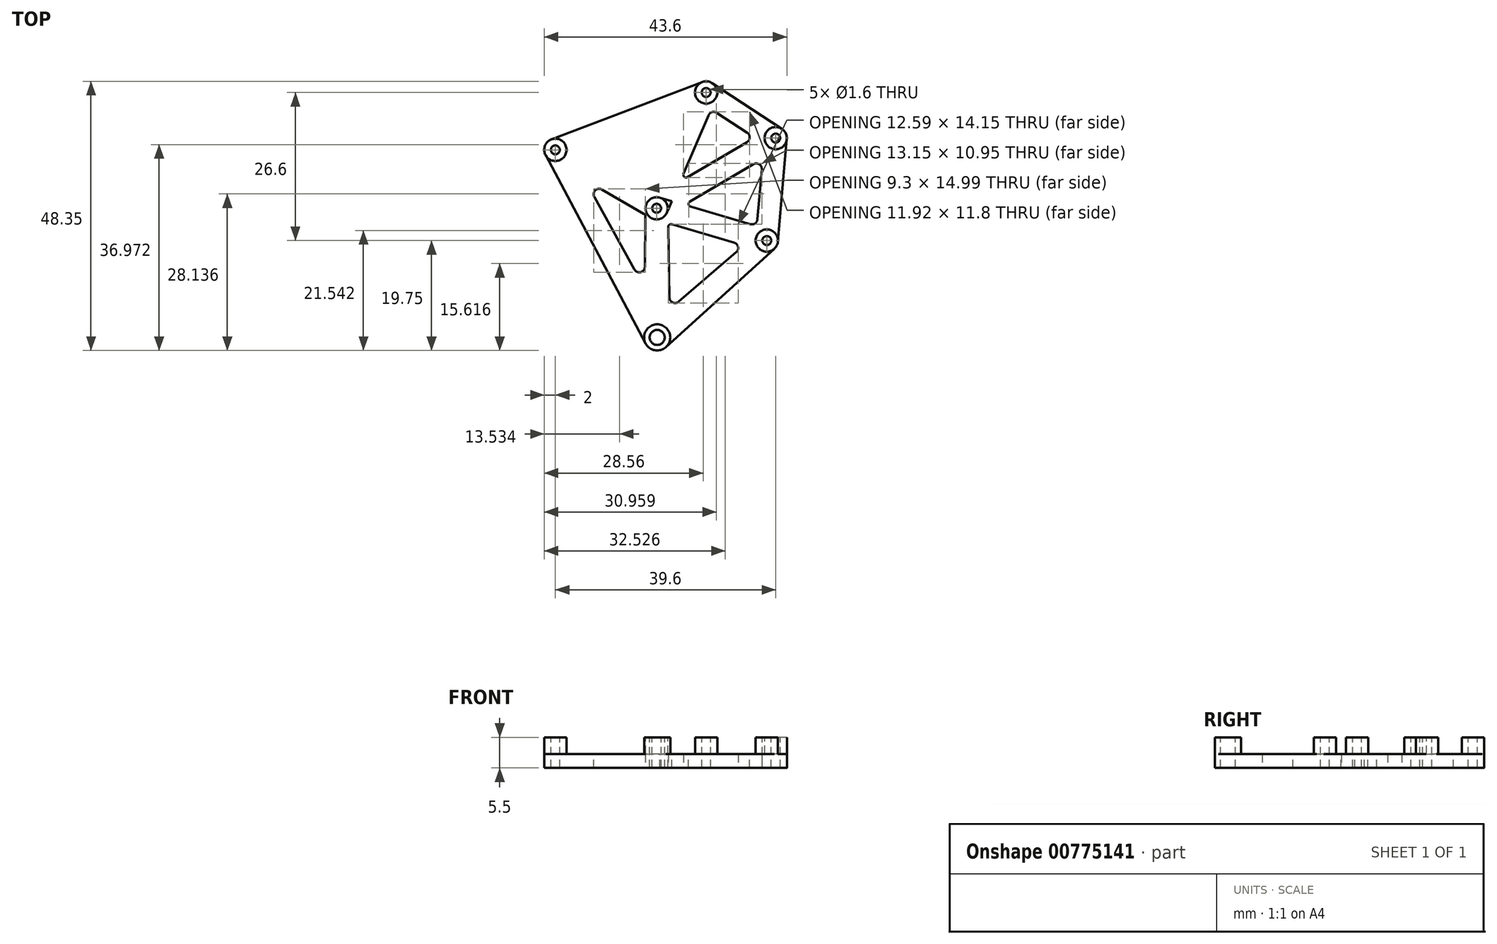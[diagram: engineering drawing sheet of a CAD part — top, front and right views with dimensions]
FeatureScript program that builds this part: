
annotation { "Feature Type Name" : "Feature", "Feature Type Description" : "" }
export const myFeature = defineFeature(function(context is Context, id is Id, definition is map)
    precondition{}
    {
        {
            var Q0;
            Q0=qCreatedBy(makeId("Top.planeOp"),FACE);
            var sketch = newSketch(context, id + "F0", { "sketchPlane" : qUnion([Q0])});
            skCircle(sketch, "E0", {"center": v(4.2, 40) * mm, "radius": 0.8 * mm});
            skCircle(sketch, "E1", {"center": v(31.3, 50.3) * mm, "radius": 0.8 * mm});
            skCircle(sketch, "E2", {"center": v(43.8, 42.1) * mm, "radius": 0.8 * mm});
            skCircle(sketch, "E3", {"center": v(22.4, 29.5) * mm, "radius": 0.8 * mm});
            skCircle(sketch, "E4", {"center": v(22.5, 6.3) * mm, "radius": 1.35 * mm});
            skCircle(sketch, "E5", {"center": v(42.2, 23.7) * mm, "radius": 0.8 * mm});
            skSolve(sketch);
        }
        {
            var Q0;
            Q0=qCreatedBy(makeId("Top.planeOp"),FACE);
            var sketch = newSketch(context, id + "F1", { "sketchPlane" : qUnion([Q0])});
            skCircle(sketch, "E6.0", {"center": v(4.2, 40) * mm, "radius": 0.8 * mm});
            skPoint(sketch, "E7.0", {"position": v(22.4, 29.5) * mm});
            skPoint(sketch, "E8.0", {"position": v(31.3, 50.3) * mm});
            skCircle(sketch, "E9.0", {"center": v(31.3, 50.3) * mm, "radius": 0.8 * mm});
            skCircle(sketch, "E10.0", {"center": v(43.8, 42.1) * mm, "radius": 0.8 * mm});
            skCircle(sketch, "E11.0", {"center": v(22.4, 29.5) * mm, "radius": 0.8 * mm});
            skCircle(sketch, "E12.0", {"center": v(42.2, 23.7) * mm, "radius": 0.8 * mm});
            skCircle(sketch, "E13.0", {"center": v(22.5, 6.3) * mm, "radius": 1.35 * mm});
            skLineSegment(sketch, "E14", {"start": v(4.2, 40) * mm, "end": v(22.4, 29.5) * mm, "construction": true});
            skLineSegment(sketch, "E15", {"start": v(31.3, 50.3) * mm, "end": v(22.4, 29.5) * mm, "construction": true});
            skLineSegment(sketch, "E16", {"start": v(22.4, 29.5) * mm, "end": v(42.2, 23.7) * mm, "construction": true});
            skLineSegment(sketch, "E17", {"start": v(22.4, 29.5) * mm, "end": v(22.5, 6.3) * mm, "construction": true});
            skLineSegment(sketch, "E18", {"start": v(22.4, 29.5) * mm, "end": v(43.8, 42.1) * mm, "construction": true});
            skLineSegment(sketch, "E19", {"start": v(43.8, 42.1) * mm, "end": v(42.2, 23.7) * mm, "construction": true});
            skLineSegment(sketch, "E20", {"start": v(22.5, 6.3) * mm, "end": v(42.2, 23.7) * mm, "construction": true});
            skLineSegment(sketch, "E21", {"start": v(43.8, 42.1) * mm, "end": v(31.3, 50.3) * mm});
            skLineSegment(sketch, "E22", {"start": v(31.3, 50.3) * mm, "end": v(4.2, 40) * mm, "construction": true});
            skLineSegment(sketch, "E23", {"start": v(4.2, 40) * mm, "end": v(22.5, 6.3) * mm, "construction": true});
            skLineSegment(sketch, "E24", {"start": v(5.2, 41.73) * mm, "end": v(23.4, 31.23) * mm});
            skLineSegment(sketch, "E25", {"start": v(3.2, 38.27) * mm, "end": v(21.4, 27.77) * mm});
            skArc(sketch, "E26", {"start": v(5.2, 41.73) * mm, "mid": v(2.47, 41) * mm, "end": v(3.2, 38.27) * mm});
            skArc(sketch, "E27", {"start": v(21.4, 27.77) * mm, "mid": v(24.13, 28.5) * mm, "end": v(23.4, 31.23) * mm});
            skLineSegment(sketch, "E28", {"start": v(20.4, 29.52) * mm, "end": v(20.15, 6.33) * mm});
            skLineSegment(sketch, "E29", {"start": v(24.4, 29.54) * mm, "end": v(24.85, 6.35) * mm});
            skArc(sketch, "E30", {"start": v(20.15, 6.33) * mm, "mid": v(20.22, 5.74) * mm, "end": v(20.42, 5.2) * mm});
            skArc(sketch, "E31", {"start": v(20.4, 29.52) * mm, "mid": v(22.4, 31.5) * mm, "end": v(24.4, 29.54) * mm});
            skLineSegment(sketch, "E32", {"start": v(2.43, 39.06) * mm, "end": v(20.42, 5.2) * mm});
            skCircle(sketch, "E33", {"center": v(22.5, 6.3) * mm, "radius": 2.35 * mm});
            skCircle(sketch, "E34", {"center": v(4.2, 40) * mm, "radius": 2 * mm});
            skLineSegment(sketch, "E35", {"start": v(5.95, 40.97) * mm, "end": v(24.55, 7.44) * mm});
            skCircle(sketch, "E36", {"center": v(42.2, 23.7) * mm, "radius": 2 * mm});
            skCircle(sketch, "E37", {"center": v(22.4, 29.5) * mm, "radius": 2 * mm});
            skLineSegment(sketch, "E38", {"start": v(42.76, 25.62) * mm, "end": v(22.96, 31.42) * mm});
            skLineSegment(sketch, "E39", {"start": v(41.64, 21.78) * mm, "end": v(21.84, 27.58) * mm});
            skLineSegment(sketch, "E40", {"start": v(24.08, 4.56) * mm, "end": v(43.54, 22.22) * mm});
            skLineSegment(sketch, "E41", {"start": v(20.97, 8.08) * mm, "end": v(40.9, 25.22) * mm});
            skCircle(sketch, "E42", {"center": v(43.8, 42.1) * mm, "radius": 2 * mm});
            skCircle(sketch, "E43", {"center": v(31.3, 50.3) * mm, "radius": 2 * mm});
            skLineSegment(sketch, "E44", {"start": v(45.8, 41.93) * mm, "end": v(44.2, 23.53) * mm});
            skLineSegment(sketch, "E45", {"start": v(40.2, 23.87) * mm, "end": v(41.8, 42.27) * mm});
            skLineSegment(sketch, "E46", {"start": v(32.4, 51.97) * mm, "end": v(44.9, 43.77) * mm});
            skLineSegment(sketch, "E47", {"start": v(30.2, 48.63) * mm, "end": v(42.7, 40.43) * mm});
            skLineSegment(sketch, "E48", {"start": v(21.39, 31.22) * mm, "end": v(42.79, 43.82) * mm});
            skLineSegment(sketch, "E49", {"start": v(44.81, 40.38) * mm, "end": v(23.41, 27.78) * mm});
            skLineSegment(sketch, "E50", {"start": v(29.46, 51.09) * mm, "end": v(20.56, 30.29) * mm});
            skLineSegment(sketch, "E51", {"start": v(33.14, 49.51) * mm, "end": v(24.24, 28.71) * mm});
            skLineSegment(sketch, "E52", {"start": v(5.15, 38.24) * mm, "end": v(32, 48.43) * mm});
            skLineSegment(sketch, "E53", {"start": v(3.49, 41.87) * mm, "end": v(30.59, 52.17) * mm});
            skPoint(sketch, "E54.end.orphan", {"position": v(23.62, 4.23) * mm});
            skArc(sketch, "E55.trimOffspring", {"start": v(24.08, 4.56) * mm, "mid": v(24.66, 5.37) * mm, "end": v(24.85, 6.35) * mm});
            skPoint(sketch, "E56.end.orphan", {"position": v(23.14, 5.11) * mm});
            skSolve(sketch);
        }
        {
            var Q0;
            Q0=makeQuery(id+"F1.imprint","IMPRINT",FACE,{"disambiguationData":[TD([[makeQuery(id+"F1.imprint","IMPRINT",EDGE,{"derivedFrom":sQuery(id+"F1.wireOp",EDGE,"E6.0")}),-1.0]])]});
            var Q1;
            {var subQ3=sQuery(id+"F1.wireOp",EDGE,"E53");Q1=makeQuery(id+"F1.imprint","IMPRINT",FACE,{"disambiguationData":[TD([[makeQuery(id+"F1.imprint","IMPRINT",EDGE,{"derivedFrom":subQ3}),-1.0]])]});}
            var Q2;
            Q2=makeQuery(id+"F1.imprint","IMPRINT",FACE,{"disambiguationData":[TD([[makeQuery(id+"F1.imprint","IMPRINT",EDGE,{"derivedFrom":sQuery(id+"F1.wireOp",EDGE,"E9.0")}),-1.0]])]});
            var Q3;
            Q3=makeQuery(id+"F1.imprint","IMPRINT",FACE,{"disambiguationData":[TD([[makeQuery(id+"F1.imprint","IMPRINT",EDGE,{"derivedFrom":sQuery(id+"F1.wireOp",EDGE,"E13.0")}),-1.0]])]});
            var Q4;
            Q4=makeQuery(id+"F1.imprint","IMPRINT",FACE,{"disambiguationData":[TD([[makeQuery(id+"F1.imprint","IMPRINT",EDGE,{"derivedFrom":sQuery(id+"F1.wireOp",EDGE,"E12.0")}),-1.0]])]});
            var Q5;
            Q5=makeQuery(id+"F1.imprint","IMPRINT",FACE,{"disambiguationData":[TD([[makeQuery(id+"F1.imprint","IMPRINT",EDGE,{"derivedFrom":sQuery(id+"F1.wireOp",EDGE,"E10.0")}),-1.0]])]});
            var Q6;
            Q6=makeQuery(id+"F1.imprint","IMPRINT",FACE,{"disambiguationData":[TD([[makeQuery(id+"F1.imprint","IMPRINT",EDGE,{"derivedFrom":sQuery(id+"F1.wireOp",EDGE,"E11.0")}),-1.0]])]});
            var Q7;
            {var subQ3=sQuery(id+"F1.wireOp",EDGE,"E40");Q7=makeQuery(id+"F1.imprint","IMPRINT",FACE,{"disambiguationData":[TD([[makeQuery(id+"F1.imprint","IMPRINT",EDGE,{"derivedFrom":subQ3}),1.0]])]});}
            var Q8;
            {var subQ0=sQuery(id+"F1.wireOp",EDGE,"E44");Q8=makeQuery(id+"F1.imprint","IMPRINT",FACE,{"disambiguationData":[TD([[makeQuery(id+"F1.imprint","IMPRINT",EDGE,{"derivedFrom":subQ0}),-1.0]])]});}
            var Q9;
            {var subQ0=sQuery(id+"F1.wireOp",EDGE,"E33");var subQ1=sQuery(id+"F1.wireOp",EDGE,"E29");var subQ2=makeQuery(id+"F1.imprint","INTERSECT",VERTEX,{"derivedFrom":[subQ1,subQ0]});Q9=makeQuery(id+"F1.imprint","IMPRINT",FACE,{"disambiguationData":[TD([[makeQuery(id+"F1.imprint","IMPRINT",EDGE,{"disambiguationData":[TD([[subQ2,1.0]])],"derivedFrom":subQ1}),-1.0]])]});}
            var Q10;
            {var subQ0=sQuery(id+"F1.wireOp",EDGE,"E35");var subQ1=sQuery(id+"F1.wireOp",EDGE,"E33");var subQ2=makeQuery(id+"F1.imprint","INTERSECT",VERTEX,{"derivedFrom":[subQ1,subQ0]});Q10=makeQuery(id+"F1.imprint","IMPRINT",FACE,{"disambiguationData":[TD([[makeQuery(id+"F1.imprint","IMPRINT",EDGE,{"disambiguationData":[TD([[subQ2,-1.0]])],"derivedFrom":subQ1}),-1.0]])]});}
            var Q11;
            {var subQ0=sQuery(id+"F1.wireOp",EDGE,"E39");var subQ1=sQuery(id+"F1.wireOp",EDGE,"E36");var subQ2=makeQuery(id+"F1.imprint","INTERSECT",VERTEX,{"derivedFrom":[subQ1,subQ0]});Q11=makeQuery(id+"F1.imprint","IMPRINT",FACE,{"disambiguationData":[TD([[makeQuery(id+"F1.imprint","IMPRINT",EDGE,{"disambiguationData":[TD([[subQ2,1.0]])],"derivedFrom":subQ1}),-1.0]])]});}
            var Q12;
            {var subQ0=sQuery(id+"F1.wireOp",EDGE,"E38");var subQ1=sQuery(id+"F1.wireOp",EDGE,"E36");var subQ2=makeQuery(id+"F1.imprint","INTERSECT",VERTEX,{"derivedFrom":[subQ1,subQ0]});Q12=makeQuery(id+"F1.imprint","IMPRINT",FACE,{"disambiguationData":[TD([[makeQuery(id+"F1.imprint","IMPRINT",EDGE,{"disambiguationData":[TD([[subQ2,-1.0]])],"derivedFrom":subQ1}),-1.0]])]});}
            var Q13;
            {var subQ0=sQuery(id+"F1.wireOp",EDGE,"E47");var subQ1=sQuery(id+"F1.wireOp",EDGE,"E42");var subQ2=makeQuery(id+"F1.imprint","INTERSECT",VERTEX,{"derivedFrom":[subQ1,subQ0]});Q13=makeQuery(id+"F1.imprint","IMPRINT",FACE,{"disambiguationData":[TD([[makeQuery(id+"F1.imprint","IMPRINT",EDGE,{"disambiguationData":[TD([[subQ2,-1.0]])],"derivedFrom":subQ1}),-1.0]])]});}
            var Q14;
            {var subQ0=sQuery(id+"F1.wireOp",EDGE,"E45");var subQ1=sQuery(id+"F1.wireOp",EDGE,"E42");var subQ2=makeQuery(id+"F1.imprint","INTERSECT",VERTEX,{"derivedFrom":[subQ1,subQ0]});Q14=makeQuery(id+"F1.imprint","IMPRINT",FACE,{"disambiguationData":[TD([[makeQuery(id+"F1.imprint","IMPRINT",EDGE,{"disambiguationData":[TD([[subQ2,-1.0]])],"derivedFrom":subQ1}),-1.0]])]});}
            var Q15;
            {var subQ0=sQuery(id+"F1.wireOp",EDGE,"E41");var subQ1=sQuery(id+"F1.wireOp",EDGE,"E36");var subQ2=makeQuery(id+"F1.imprint","INTERSECT",VERTEX,{"derivedFrom":[subQ1,subQ0]});Q15=makeQuery(id+"F1.imprint","IMPRINT",FACE,{"disambiguationData":[TD([[makeQuery(id+"F1.imprint","IMPRINT",EDGE,{"disambiguationData":[TD([[subQ2,-1.0]])],"derivedFrom":subQ1}),-1.0]])]});}
            var Q16;
            {var subQ3=sQuery(id+"F1.wireOp",EDGE,"E32");Q16=makeQuery(id+"F1.imprint","IMPRINT",FACE,{"disambiguationData":[TD([[makeQuery(id+"F1.imprint","IMPRINT",EDGE,{"derivedFrom":subQ3}),1.0]])]});}
            var Q17;
            {var subQ0=sQuery(id+"F1.wireOp",EDGE,"E33");var subQ1=sQuery(id+"F1.wireOp",EDGE,"E28");var subQ2=makeQuery(id+"F1.imprint","INTERSECT",VERTEX,{"derivedFrom":[subQ1,subQ0]});Q17=makeQuery(id+"F1.imprint","IMPRINT",FACE,{"disambiguationData":[TD([[makeQuery(id+"F1.imprint","IMPRINT",EDGE,{"disambiguationData":[TD([[subQ2,1.0]])],"derivedFrom":subQ1}),1.0]])]});}
            var Q18;
            {var subQ6=sQuery(id+"F1.wireOp",EDGE,"E25");var subQ11=sQuery(id+"F1.wireOp",EDGE,"E37");var subQ12=makeQuery(id+"F1.imprint","INTERSECT",VERTEX,{"derivedFrom":[subQ6,subQ11]});Q18=makeQuery(id+"F1.imprint","IMPRINT",FACE,{"disambiguationData":[TD([[makeQuery(id+"F1.imprint","IMPRINT",EDGE,{"disambiguationData":[TD([[subQ12,1.0]])],"derivedFrom":subQ6}),-1.0]])]});}
            var Q19;
            {var subQ0=sQuery(id+"F1.wireOp",EDGE,"E46");Q19=makeQuery(id+"F1.imprint","IMPRINT",FACE,{"disambiguationData":[TD([[makeQuery(id+"F1.imprint","IMPRINT",EDGE,{"derivedFrom":subQ0}),-1.0]])]});}
            var Q20;
            {var subQ0=sQuery(id+"F1.wireOp",EDGE,"E48");var subQ1=sQuery(id+"F1.wireOp",EDGE,"E21");var subQ2=makeQuery(id+"F1.imprint","INTERSECT",VERTEX,{"derivedFrom":[subQ1,subQ0]});Q20=makeQuery(id+"F1.imprint","IMPRINT",FACE,{"disambiguationData":[TD([[makeQuery(id+"F1.imprint","IMPRINT",EDGE,{"disambiguationData":[TD([[subQ2,-1.0]])],"derivedFrom":subQ1}),1.0]])]});}
            var Q21;
            {var subQ5=sQuery(id+"F1.wireOp",EDGE,"E42");var subQ7=sQuery(id+"F1.wireOp",EDGE,"E21");var subQ8=makeQuery(id+"F1.imprint","INTERSECT",VERTEX,{"derivedFrom":[subQ7,subQ5]});Q21=makeQuery(id+"F1.imprint","IMPRINT",FACE,{"disambiguationData":[TD([[makeQuery(id+"F1.imprint","IMPRINT",EDGE,{"disambiguationData":[TD([[subQ8,-1.0]])],"derivedFrom":subQ7}),1.0]])]});}
            var Q22;
            {var subQ0=sQuery(id+"F1.wireOp",EDGE,"E42");var subQ1=sQuery(id+"F1.wireOp",EDGE,"E21");var subQ2=makeQuery(id+"F1.imprint","INTERSECT",VERTEX,{"derivedFrom":[subQ1,subQ0]});Q22=makeQuery(id+"F1.imprint","IMPRINT",FACE,{"disambiguationData":[TD([[makeQuery(id+"F1.imprint","IMPRINT",EDGE,{"disambiguationData":[TD([[subQ2,-1.0]])],"derivedFrom":subQ1}),-1.0]])]});}
            var Q23;
            {var subQ1=sQuery(id+"F1.wireOp",EDGE,"E21");var subQ7=sQuery(id+"F1.wireOp",EDGE,"E43");var subQ9=makeQuery(id+"F1.imprint","INTERSECT",VERTEX,{"derivedFrom":[subQ1,subQ7]});Q23=makeQuery(id+"F1.imprint","IMPRINT",FACE,{"disambiguationData":[TD([[makeQuery(id+"F1.imprint","IMPRINT",EDGE,{"disambiguationData":[TD([[subQ9,1.0]])],"derivedFrom":subQ1}),1.0]])]});}
            var Q24;
            {var subQ0=sQuery(id+"F1.wireOp",EDGE,"E43");var subQ1=sQuery(id+"F1.wireOp",EDGE,"E21");var subQ2=makeQuery(id+"F1.imprint","INTERSECT",VERTEX,{"derivedFrom":[subQ1,subQ0]});Q24=makeQuery(id+"F1.imprint","IMPRINT",FACE,{"disambiguationData":[TD([[makeQuery(id+"F1.imprint","IMPRINT",EDGE,{"disambiguationData":[TD([[subQ2,1.0]])],"derivedFrom":subQ1}),-1.0]])]});}
            var Q25;
            {var subQ0=sQuery(id+"F1.wireOp",EDGE,"E47");var subQ1=sQuery(id+"F1.wireOp",EDGE,"E43");var subQ2=makeQuery(id+"F1.imprint","INTERSECT",VERTEX,{"derivedFrom":[subQ1,subQ0]});Q25=makeQuery(id+"F1.imprint","IMPRINT",FACE,{"disambiguationData":[TD([[makeQuery(id+"F1.imprint","IMPRINT",EDGE,{"disambiguationData":[TD([[subQ2,-1.0]])],"derivedFrom":subQ1}),-1.0]])]});}
            var Q26;
            {var subQ0=sQuery(id+"F1.wireOp",EDGE,"E47");var subQ1=sQuery(id+"F1.wireOp",EDGE,"E43");var subQ2=makeQuery(id+"F1.imprint","INTERSECT",VERTEX,{"derivedFrom":[subQ1,subQ0]});Q26=makeQuery(id+"F1.imprint","IMPRINT",FACE,{"disambiguationData":[TD([[makeQuery(id+"F1.imprint","IMPRINT",EDGE,{"disambiguationData":[TD([[subQ2,1.0]])],"derivedFrom":subQ1}),-1.0]])]});}
            var Q27;
            {var subQ0=sQuery(id+"F1.wireOp",EDGE,"E34");var subQ1=sQuery(id+"F1.wireOp",EDGE,"E24");var subQ2=makeQuery(id+"F1.imprint","INTERSECT",VERTEX,{"derivedFrom":[subQ1,subQ0]});Q27=makeQuery(id+"F1.imprint","IMPRINT",FACE,{"disambiguationData":[TD([[makeQuery(id+"F1.imprint","IMPRINT",EDGE,{"disambiguationData":[TD([[subQ2,-1.0]])],"derivedFrom":subQ1}),-1.0]])]});}
            var Q28;
            {var subQ0=sQuery(id+"F1.wireOp",EDGE,"E35");var subQ1=sQuery(id+"F1.wireOp",EDGE,"E34");var subQ2=makeQuery(id+"F1.imprint","INTERSECT",VERTEX,{"derivedFrom":[subQ1,subQ0]});Q28=makeQuery(id+"F1.imprint","IMPRINT",FACE,{"disambiguationData":[TD([[makeQuery(id+"F1.imprint","IMPRINT",EDGE,{"disambiguationData":[TD([[subQ2,1.0]])],"derivedFrom":subQ1}),-1.0]])]});}
            var Q29;
            {var subQ0=sQuery(id+"F1.wireOp",EDGE,"E34");var subQ1=sQuery(id+"F1.wireOp",EDGE,"E25");var subQ2=makeQuery(id+"F1.imprint","INTERSECT",VERTEX,{"derivedFrom":[subQ1,subQ0]});Q29=makeQuery(id+"F1.imprint","IMPRINT",FACE,{"disambiguationData":[TD([[makeQuery(id+"F1.imprint","IMPRINT",EDGE,{"disambiguationData":[TD([[subQ2,-1.0]])],"derivedFrom":subQ1}),1.0]])]});}
            var Q30;
            {var subQ3=sQuery(id+"F1.wireOp",EDGE,"E52");var subQ9=sQuery(id+"F1.wireOp",EDGE,"E24");var subQ10=makeQuery(id+"F1.imprint","INTERSECT",VERTEX,{"derivedFrom":[subQ9,subQ3]});Q30=makeQuery(id+"F1.imprint","IMPRINT",FACE,{"disambiguationData":[TD([[makeQuery(id+"F1.imprint","IMPRINT",EDGE,{"disambiguationData":[TD([[subQ10,-1.0]])],"derivedFrom":subQ9}),-1.0]])]});}
            var Q31;
            {var subQ0=sQuery(id+"F1.wireOp",EDGE,"E50");var subQ1=sQuery(id+"F1.wireOp",EDGE,"E24");var subQ2=makeQuery(id+"F1.imprint","INTERSECT",VERTEX,{"derivedFrom":[subQ1,subQ0]});Q31=makeQuery(id+"F1.imprint","IMPRINT",FACE,{"disambiguationData":[TD([[makeQuery(id+"F1.imprint","IMPRINT",EDGE,{"disambiguationData":[TD([[subQ2,-1.0]])],"derivedFrom":subQ1}),-1.0]])]});}
            var Q32;
            {var subQ0=sQuery(id+"F1.wireOp",EDGE,"E50");var subQ1=sQuery(id+"F1.wireOp",EDGE,"E24");var subQ2=makeQuery(id+"F1.imprint","INTERSECT",VERTEX,{"derivedFrom":[subQ1,subQ0]});Q32=makeQuery(id+"F1.imprint","IMPRINT",FACE,{"disambiguationData":[TD([[makeQuery(id+"F1.imprint","IMPRINT",EDGE,{"disambiguationData":[TD([[subQ2,-1.0]])],"derivedFrom":subQ1}),1.0]])]});}
            var Q33;
            {var subQ0=sQuery(id+"F1.wireOp",EDGE,"E48");var subQ1=sQuery(id+"F1.wireOp",EDGE,"E24");var subQ2=makeQuery(id+"F1.imprint","INTERSECT",VERTEX,{"derivedFrom":[subQ1,subQ0]});Q33=makeQuery(id+"F1.imprint","IMPRINT",FACE,{"disambiguationData":[TD([[makeQuery(id+"F1.imprint","IMPRINT",EDGE,{"disambiguationData":[TD([[subQ2,-1.0]])],"derivedFrom":subQ1}),1.0]])]});}
            var Q34;
            {var subQ7=sQuery(id+"F1.wireOp",EDGE,"E49");var subQ9=sQuery(id+"F1.wireOp",EDGE,"E29");var subQ11=makeQuery(id+"F1.imprint","INTERSECT",VERTEX,{"derivedFrom":[subQ9,subQ7]});Q34=makeQuery(id+"F1.imprint","IMPRINT",FACE,{"disambiguationData":[TD([[makeQuery(id+"F1.imprint","IMPRINT",EDGE,{"disambiguationData":[TD([[subQ11,-1.0]])],"derivedFrom":subQ9}),1.0]])]});}
            var Q35;
            {var subQ0=sQuery(id+"F1.wireOp",EDGE,"E51");var subQ1=sQuery(id+"F1.wireOp",EDGE,"E29");var subQ2=makeQuery(id+"F1.imprint","INTERSECT",VERTEX,{"derivedFrom":[subQ1,subQ0]});Q35=makeQuery(id+"F1.imprint","IMPRINT",FACE,{"disambiguationData":[TD([[makeQuery(id+"F1.imprint","IMPRINT",EDGE,{"disambiguationData":[TD([[subQ2,-1.0]])],"derivedFrom":subQ1}),1.0]])]});}
            var Q36;
            {var subQ0=sQuery(id+"F1.wireOp",EDGE,"E37");var subQ1=sQuery(id+"F1.wireOp",EDGE,"E25");var subQ2=makeQuery(id+"F1.imprint","INTERSECT",VERTEX,{"derivedFrom":[subQ1,subQ0]});Q36=makeQuery(id+"F1.imprint","IMPRINT",FACE,{"disambiguationData":[TD([[makeQuery(id+"F1.imprint","IMPRINT",EDGE,{"disambiguationData":[TD([[subQ2,1.0]])],"derivedFrom":subQ1}),1.0]])]});}
            var Q37;
            {var subQ0=sQuery(id+"F1.wireOp",EDGE,"E49");var subQ1=sQuery(id+"F1.wireOp",EDGE,"E29");var subQ2=makeQuery(id+"F1.imprint","INTERSECT",VERTEX,{"derivedFrom":[subQ1,subQ0]});Q37=makeQuery(id+"F1.imprint","IMPRINT",FACE,{"disambiguationData":[TD([[makeQuery(id+"F1.imprint","IMPRINT",EDGE,{"disambiguationData":[TD([[subQ2,-1.0]])],"derivedFrom":subQ1}),-1.0]])]});}
            var Q38;
            {var subQ0=sQuery(id+"F1.wireOp",EDGE,"E51");var subQ1=sQuery(id+"F1.wireOp",EDGE,"E29");var subQ2=makeQuery(id+"F1.imprint","INTERSECT",VERTEX,{"derivedFrom":[subQ1,subQ0]});Q38=makeQuery(id+"F1.imprint","IMPRINT",FACE,{"disambiguationData":[TD([[makeQuery(id+"F1.imprint","IMPRINT",EDGE,{"disambiguationData":[TD([[subQ2,-1.0]])],"derivedFrom":subQ1}),-1.0]])]});}
            var Q39;
            {var subQ0=sQuery(id+"F1.wireOp",EDGE,"E37");var subQ1=sQuery(id+"F1.wireOp",EDGE,"E29");var subQ2=makeQuery(id+"F1.imprint","INTERSECT",VERTEX,{"derivedFrom":[subQ1,subQ0]});Q39=makeQuery(id+"F1.imprint","IMPRINT",FACE,{"disambiguationData":[TD([[makeQuery(id+"F1.imprint","IMPRINT",EDGE,{"disambiguationData":[TD([[subQ2,-1.0]])],"derivedFrom":subQ1}),-1.0]])]});}
            var Q40;
            {var subQ1=sQuery(id+"F1.wireOp",EDGE,"E24");var subQ5=sQuery(id+"F1.wireOp",EDGE,"E37");var subQ6=makeQuery(id+"F1.imprint","INTERSECT",VERTEX,{"derivedFrom":[subQ1,subQ5]});Q40=makeQuery(id+"F1.imprint","IMPRINT",FACE,{"disambiguationData":[TD([[makeQuery(id+"F1.imprint","IMPRINT",EDGE,{"disambiguationData":[TD([[subQ6,1.0]])],"derivedFrom":subQ1}),1.0]])]});}
            var Q41;
            {var subQ0=sQuery(id+"F1.wireOp",EDGE,"E48");var subQ1=sQuery(id+"F1.wireOp",EDGE,"E24");var subQ2=makeQuery(id+"F1.imprint","INTERSECT",VERTEX,{"derivedFrom":[subQ1,subQ0]});Q41=makeQuery(id+"F1.imprint","IMPRINT",FACE,{"disambiguationData":[TD([[makeQuery(id+"F1.imprint","IMPRINT",EDGE,{"disambiguationData":[TD([[subQ2,-1.0]])],"derivedFrom":subQ1}),-1.0]])]});}
            var Q42;
            {var subQ0=sQuery(id+"F1.wireOp",EDGE,"E37");var subQ1=sQuery(id+"F1.wireOp",EDGE,"E24");var subQ2=makeQuery(id+"F1.imprint","INTERSECT",VERTEX,{"derivedFrom":[subQ1,subQ0]});Q42=makeQuery(id+"F1.imprint","IMPRINT",FACE,{"disambiguationData":[TD([[makeQuery(id+"F1.imprint","IMPRINT",EDGE,{"disambiguationData":[TD([[subQ2,1.0]])],"derivedFrom":subQ1}),-1.0]])]});}
            var Q43;
            {var subQ7=sQuery(id+"F1.wireOp",EDGE,"E49");var subQ9=sQuery(id+"F1.wireOp",EDGE,"E38");var subQ10=makeQuery(id+"F1.imprint","INTERSECT",VERTEX,{"derivedFrom":[subQ9,subQ7]});Q43=makeQuery(id+"F1.imprint","IMPRINT",FACE,{"disambiguationData":[TD([[makeQuery(id+"F1.imprint","IMPRINT",EDGE,{"disambiguationData":[TD([[subQ10,-1.0]])],"derivedFrom":subQ9}),-1.0]])]});}
            extrude(context, id + "F2", {"entities" : qUnion([Q0, Q1, Q2, Q3, Q4, Q5, Q6, Q7, Q8, Q9, Q10, Q11, Q12, Q13, Q14, Q15, Q16, Q17, Q18, Q19, Q20, Q21, Q22, Q23, Q24, Q25, Q26, Q27, Q28, Q29, Q30, Q31, Q32, Q33, Q34, Q35, Q36, Q37, Q38, Q39, Q40, Q41, Q42, Q43]), "oppositeDirection" : true, "depth" : 2.5 * mm, "offsetDistance" : 25 * mm});
        }
        {
            var Q0;
            Q0=makeQuery(id+"F1.imprint","IMPRINT",FACE,{"disambiguationData":[TD([[makeQuery(id+"F1.imprint","IMPRINT",EDGE,{"derivedFrom":sQuery(id+"F1.wireOp",EDGE,"E6.0")}),-1.0]])]});
            var Q1;
            Q1=makeQuery(id+"F1.imprint","IMPRINT",FACE,{"disambiguationData":[TD([[makeQuery(id+"F1.imprint","IMPRINT",EDGE,{"derivedFrom":sQuery(id+"F1.wireOp",EDGE,"E9.0")}),-1.0]])]});
            var Q2;
            Q2=makeQuery(id+"F1.imprint","IMPRINT",FACE,{"disambiguationData":[TD([[makeQuery(id+"F1.imprint","IMPRINT",EDGE,{"derivedFrom":sQuery(id+"F1.wireOp",EDGE,"E11.0")}),-1.0]])]});
            var Q3;
            Q3=makeQuery(id+"F1.imprint","IMPRINT",FACE,{"disambiguationData":[TD([[makeQuery(id+"F1.imprint","IMPRINT",EDGE,{"derivedFrom":sQuery(id+"F1.wireOp",EDGE,"E10.0")}),-1.0]])]});
            var Q4;
            Q4=makeQuery(id+"F1.imprint","IMPRINT",FACE,{"disambiguationData":[TD([[makeQuery(id+"F1.imprint","IMPRINT",EDGE,{"derivedFrom":sQuery(id+"F1.wireOp",EDGE,"E12.0")}),-1.0]])]});
            var Q5;
            Q5=makeQuery(id+"F1.imprint","IMPRINT",FACE,{"disambiguationData":[TD([[makeQuery(id+"F1.imprint","IMPRINT",EDGE,{"derivedFrom":sQuery(id+"F1.wireOp",EDGE,"E13.0")}),-1.0]])]});
            extrude(context, id + "F3", {"entities" : qUnion([Q0, Q1, Q2, Q3, Q4, Q5]), "operationType" : NewBodyOperationType.ADD, "depth" : 3 * mm, "offsetDistance" : 25 * mm});
        }
        {
            var Q0;
            Q0=makeQuery(id+"F2.opExtrude","SWEPT_EDGE",EDGE,{"disambiguationData":[OSD([sQuery(id+"F1.wireOp",EDGE,"E24"),sQuery(id+"F1.wireOp",EDGE,"E52")])]});
            var Q1;
            Q1=makeQuery(id+"F2.opExtrude","SWEPT_EDGE",EDGE,{"disambiguationData":[OSD([sQuery(id+"F1.wireOp",EDGE,"E25"),sQuery(id+"F1.wireOp",EDGE,"E35")])]});
            var Q2;
            Q2=makeQuery(id+"F2.opExtrude","SWEPT_EDGE",EDGE,{"disambiguationData":[OSD([sQuery(id+"F1.wireOp",EDGE,"E28"),sQuery(id+"F1.wireOp",EDGE,"E35")])]});
            var Q3;
            Q3=makeQuery(id+"F2.opExtrude","SWEPT_EDGE",EDGE,{"disambiguationData":[OSD([sQuery(id+"F1.wireOp",EDGE,"E29"),sQuery(id+"F1.wireOp",EDGE,"E41")])]});
            var Q4;
            Q4=makeQuery(id+"F2.opExtrude","SWEPT_EDGE",EDGE,{"disambiguationData":[OSD([sQuery(id+"F1.wireOp",EDGE,"E39"),sQuery(id+"F1.wireOp",EDGE,"E41")])]});
            var Q5;
            Q5=makeQuery(id+"F2.opExtrude","SWEPT_EDGE",EDGE,{"disambiguationData":[OSD([sQuery(id+"F1.wireOp",EDGE,"E38"),sQuery(id+"F1.wireOp",EDGE,"E45")])]});
            var Q6;
            Q6=makeQuery(id+"F2.opExtrude","SWEPT_EDGE",EDGE,{"disambiguationData":[OSD([sQuery(id+"F1.wireOp",EDGE,"E45"),sQuery(id+"F1.wireOp",EDGE,"E49")])]});
            var Q7;
            Q7=makeQuery(id+"F2.opExtrude","SWEPT_EDGE",EDGE,{"disambiguationData":[OSD([sQuery(id+"F1.wireOp",EDGE,"E47"),sQuery(id+"F1.wireOp",EDGE,"E48")])]});
            var Q8;
            Q8=makeQuery(id+"F2.opExtrude","SWEPT_EDGE",EDGE,{"disambiguationData":[OSD([sQuery(id+"F1.wireOp",EDGE,"E47"),sQuery(id+"F1.wireOp",EDGE,"E51")])]});
            var Q9;
            Q9=makeQuery(id+"F2.opExtrude","SWEPT_EDGE",EDGE,{"disambiguationData":[OSD([sQuery(id+"F1.wireOp",EDGE,"E50"),sQuery(id+"F1.wireOp",EDGE,"E52")])]});
            fillet(context, id + "F4", {"entities" : qUnion([Q0, Q1, Q2, Q3, Q4, Q5, Q6, Q7, Q8, Q9]), "radius" : 1 * mm, "tangentPropagation" : true, "allowEdgeOverflow" : false});
        }
        {
            var Q0;
            Q0=makeQuery(id+"F2.opExtrude","SWEPT_EDGE",EDGE,{"disambiguationData":[OSD([sQuery(id+"F1.wireOp",EDGE,"E25"),sQuery(id+"F1.wireOp",EDGE,"E28")])]});
            var Q1;
            Q1=makeQuery(id+"F2.opExtrude","SWEPT_EDGE",EDGE,{"disambiguationData":[OSD([sQuery(id+"F1.wireOp",EDGE,"E48"),sQuery(id+"F1.wireOp",EDGE,"E51")])]});
            var Q2;
            Q2=makeQuery(id+"F2.opExtrude","SWEPT_EDGE",EDGE,{"disambiguationData":[OSD([sQuery(id+"F1.wireOp",EDGE,"E38"),sQuery(id+"F1.wireOp",EDGE,"E49")])]});
            var Q3;
            Q3=makeQuery(id+"F2.opExtrude","SWEPT_EDGE",EDGE,{"disambiguationData":[OSD([sQuery(id+"F1.wireOp",EDGE,"E29"),sQuery(id+"F1.wireOp",EDGE,"E39")])]});
            var Q4;
            Q4=makeQuery(id+"F2.opExtrude","SWEPT_EDGE",EDGE,{"disambiguationData":[OSD([sQuery(id+"F1.wireOp",EDGE,"E24"),sQuery(id+"F1.wireOp",EDGE,"E50")])]});
            fillet(context, id + "F5", {"entities" : qUnion([Q0, Q1, Q2, Q3, Q4]), "radius" : 0.5 * mm, "tangentPropagation" : true, "allowEdgeOverflow" : false});
        }
    });
